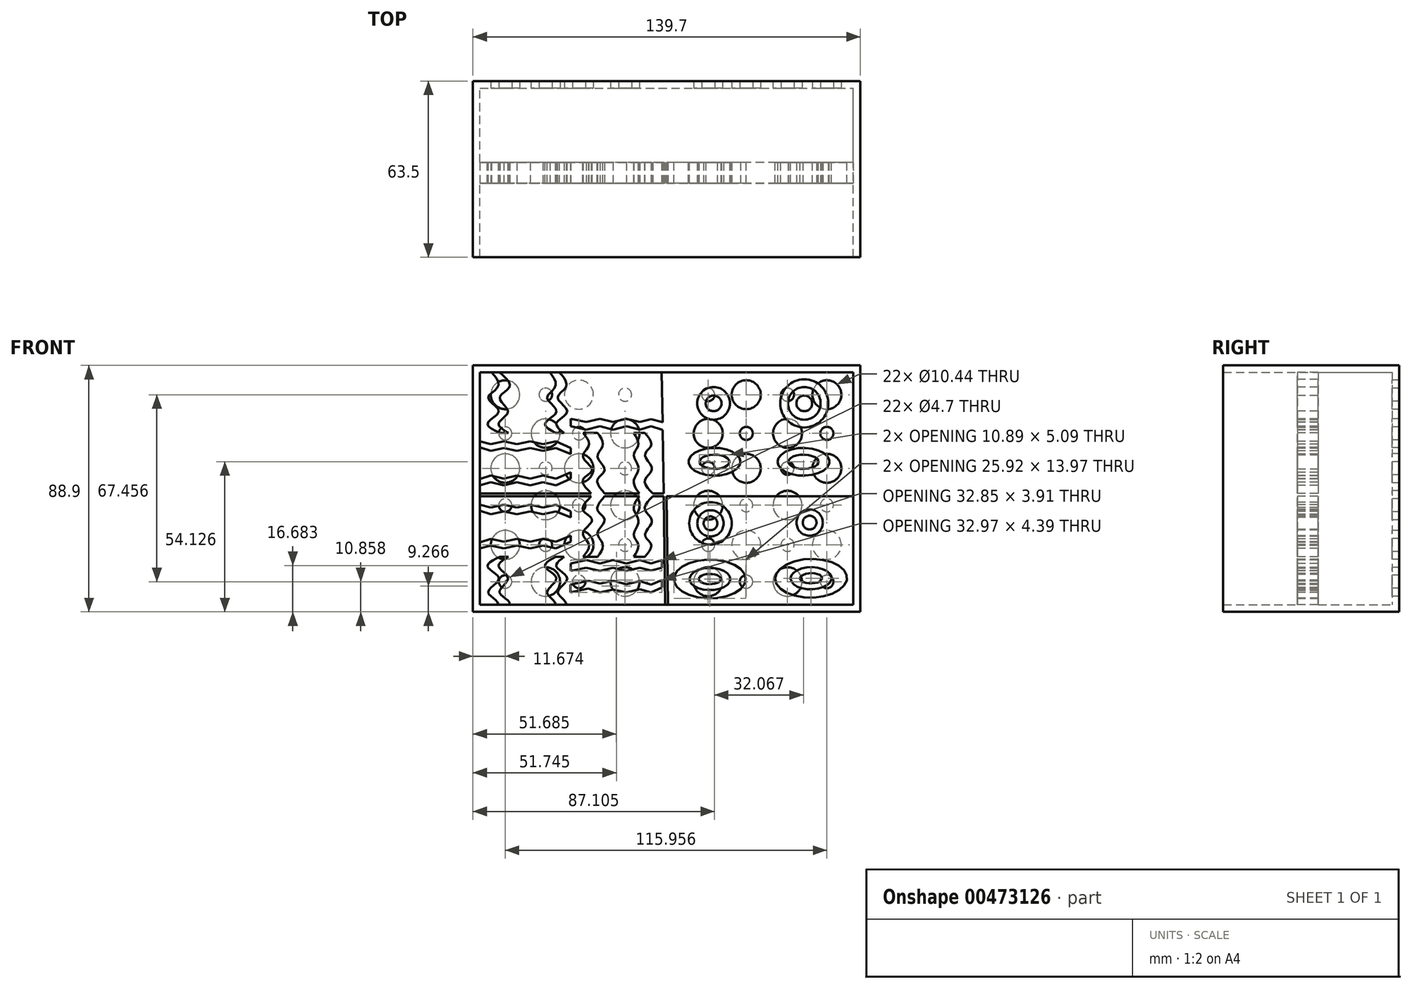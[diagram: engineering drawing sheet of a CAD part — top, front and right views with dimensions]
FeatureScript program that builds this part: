
annotation { "Feature Type Name" : "Feature", "Feature Type Description" : "" }
export const myFeature = defineFeature(function(context is Context, id is Id, definition is map)
    precondition{}
    {
        {
            var Q0;
            Q0=qCreatedBy(makeId("Front.planeOp"),FACE);
            var sketch = newSketch(context, id + "F0", { "sketchPlane" : qUnion([Q0])});
            skLineSegment(sketch, "E0.bottom", {"start": v(-68.61, 46.72) * mm, "end": v(71.09, 46.72) * mm});
            skLineSegment(sketch, "E0.top", {"start": v(-68.61, -42.18) * mm, "end": v(71.09, -42.18) * mm});
            skLineSegment(sketch, "E0.left", {"start": v(-68.61, 46.72) * mm, "end": v(-68.61, -42.18) * mm});
            skLineSegment(sketch, "E0.right", {"start": v(71.09, 46.72) * mm, "end": v(71.09, -42.18) * mm});
            skSolve(sketch);
        }
        {
            var Q0;
            Q0=makeQuery(id+"F0.imprint","IMPRINT",FACE,{"disambiguationData":[TD([[makeQuery(id+"F0.imprint","IMPRINT",EDGE,{"derivedFrom":sQuery(id+"F0.wireOp",EDGE,"E0.bottom")}),-1.0]])]});
            extrude(context, id + "F1", {"entities" : qUnion([Q0]), "depth" : 63.5 * mm});
        }
        {
            var Q0;
            Q0=makeQuery(id+"F1.opExtrude","CAP_FACE",FACE,{"disambiguationData":[OSD([sQuery(id+"F0.wireOp",EDGE,"E0.bottom"),sQuery(id+"F0.wireOp",EDGE,"E0.top"),sQuery(id+"F0.wireOp",EDGE,"E0.left"),sQuery(id+"F0.wireOp",EDGE,"E0.right")])],"isStart":false});
            shell(context, id + "F2", {"entities" : qUnion([Q0]), "thickness" : 2.54 * mm});
        }
        {
            var Q0;
            Q0=makeQuery(id+"F2.opShell","OFFSET_FACE",FACE,{"disambiguationData":[OSD([sQuery(id+"F0.wireOp",EDGE,"E0.bottom"),sQuery(id+"F0.wireOp",EDGE,"E0.top"),sQuery(id+"F0.wireOp",EDGE,"E0.left"),sQuery(id+"F0.wireOp",EDGE,"E0.right")])]});
            var sketch = newSketch(context, id + "F3", { "sketchPlane" : qUnion([Q0])});
            skLineSegment(sketch, "E1", {"start": v(-66.07, 2.27) * mm, "end": v(68.55, 2.27) * mm});
            skLineSegment(sketch, "E2", {"start": v(1.24, 44.18) * mm, "end": v(1.24, -39.64) * mm});
            skCircle(sketch, "E3", {"center": v(-56.94, 36.13) * mm, "radius": 5.21 * mm});
            skCircle(sketch, "E4", {"center": v(-42.4, 36.13) * mm, "radius": 2.36 * mm});
            skCircle(sketch, "E5", {"center": v(-30.37, 36.13) * mm, "radius": 5.22 * mm});
            skCircle(sketch, "E6", {"center": v(-13.75, 36.13) * mm, "radius": 2.36 * mm});
            skCircle(sketch, "E7", {"center": v(-56.94, 22.18) * mm, "radius": 2.35 * mm});
            skCircle(sketch, "E8", {"center": v(-42.4, 22.18) * mm, "radius": 5.22 * mm});
            skCircle(sketch, "E9", {"center": v(-30.37, 22.18) * mm, "radius": 2.35 * mm});
            skCircle(sketch, "E10", {"center": v(-13.75, 22.18) * mm, "radius": 5.22 * mm});
            skCircle(sketch, "E11", {"center": v(-56.94, 9.59) * mm, "radius": 5.22 * mm});
            skCircle(sketch, "E12", {"center": v(-42.4, 9.59) * mm, "radius": 2.35 * mm});
            skCircle(sketch, "E13", {"center": v(-30.37, 9.59) * mm, "radius": 5.22 * mm});
            skCircle(sketch, "E14", {"center": v(-13.75, 9.59) * mm, "radius": 2.35 * mm});
            skCircle(sketch, "E15", {"center": v(-56.94, -3.73) * mm, "radius": 2.35 * mm});
            skCircle(sketch, "E16", {"center": v(-42.4, -3.73) * mm, "radius": 5.22 * mm});
            skCircle(sketch, "E17", {"center": v(-30.37, -3.73) * mm, "radius": 2.35 * mm});
            skCircle(sketch, "E18", {"center": v(-13.75, -3.73) * mm, "radius": 5.22 * mm});
            skCircle(sketch, "E19", {"center": v(-56.94, -18.04) * mm, "radius": 5.22 * mm});
            skCircle(sketch, "E20", {"center": v(-42.4, -18.04) * mm, "radius": 2.35 * mm});
            skCircle(sketch, "E21", {"center": v(-30.37, -18.04) * mm, "radius": 5.22 * mm});
            skCircle(sketch, "E22", {"center": v(-13.75, -18.04) * mm, "radius": 2.35 * mm});
            skCircle(sketch, "E23", {"center": v(-56.94, -31.32) * mm, "radius": 2.35 * mm});
            skCircle(sketch, "E24", {"center": v(-42.4, -31.32) * mm, "radius": 5.22 * mm});
            skCircle(sketch, "E25", {"center": v(-30.37, -31.32) * mm, "radius": 2.35 * mm});
            skCircle(sketch, "E26", {"center": v(-13.75, -31.32) * mm, "radius": 5.22 * mm});
            skCircle(sketch, "E27", {"center": v(16.23, 36.13) * mm, "radius": 2.35 * mm});
            skCircle(sketch, "E28", {"center": v(29.95, 36.13) * mm, "radius": 5.22 * mm});
            skCircle(sketch, "E29", {"center": v(44.83, 36.13) * mm, "radius": 2.35 * mm});
            skCircle(sketch, "E30", {"center": v(59.02, 36.13) * mm, "radius": 5.22 * mm});
            skCircle(sketch, "E31", {"center": v(16.23, 22.18) * mm, "radius": 5.22 * mm});
            skCircle(sketch, "E32", {"center": v(29.95, 22.18) * mm, "radius": 2.35 * mm});
            skCircle(sketch, "E33", {"center": v(44.83, 22.18) * mm, "radius": 5.22 * mm});
            skCircle(sketch, "E34", {"center": v(59.02, 22.18) * mm, "radius": 2.35 * mm});
            skCircle(sketch, "E35", {"center": v(16.23, 9.59) * mm, "radius": 2.35 * mm});
            skCircle(sketch, "E36", {"center": v(29.95, 9.59) * mm, "radius": 5.22 * mm});
            skCircle(sketch, "E37", {"center": v(44.83, 9.59) * mm, "radius": 2.35 * mm});
            skCircle(sketch, "E38", {"center": v(59.02, 9.59) * mm, "radius": 5.22 * mm});
            skCircle(sketch, "E39", {"center": v(16.23, -3.73) * mm, "radius": 5.22 * mm});
            skCircle(sketch, "E40", {"center": v(29.95, -3.73) * mm, "radius": 2.35 * mm});
            skCircle(sketch, "E41", {"center": v(44.83, -3.73) * mm, "radius": 5.22 * mm});
            skCircle(sketch, "E42", {"center": v(59.02, -3.73) * mm, "radius": 2.35 * mm});
            skCircle(sketch, "E43", {"center": v(16.23, -18.04) * mm, "radius": 2.35 * mm});
            skCircle(sketch, "E44", {"center": v(29.95, -18.04) * mm, "radius": 5.22 * mm});
            skCircle(sketch, "E45", {"center": v(44.83, -18.04) * mm, "radius": 2.35 * mm});
            skCircle(sketch, "E46", {"center": v(59.02, -18.04) * mm, "radius": 5.22 * mm});
            skCircle(sketch, "E47", {"center": v(16.23, -31.32) * mm, "radius": 5.22 * mm});
            skCircle(sketch, "E48", {"center": v(29.95, -31.32) * mm, "radius": 2.35 * mm});
            skCircle(sketch, "E49", {"center": v(44.83, -31.32) * mm, "radius": 5.22 * mm});
            skCircle(sketch, "E50", {"center": v(59.02, -31.32) * mm, "radius": 2.35 * mm});
            skSolve(sketch);
        }
        {
            var Q0;
            Q0=makeQuery(id+"F3.imprint","IMPRINT",FACE,{"disambiguationData":[TD([[makeQuery(id+"F3.imprint","IMPRINT",EDGE,{"derivedFrom":sQuery(id+"F3.wireOp",EDGE,"E3")}),1.0]])]});
            var Q1;
            Q1=makeQuery(id+"F3.imprint","IMPRINT",FACE,{"disambiguationData":[TD([[makeQuery(id+"F3.imprint","IMPRINT",EDGE,{"derivedFrom":sQuery(id+"F3.wireOp",EDGE,"E4")}),1.0]])]});
            var Q2;
            Q2=makeQuery(id+"F3.imprint","IMPRINT",FACE,{"disambiguationData":[TD([[makeQuery(id+"F3.imprint","IMPRINT",EDGE,{"derivedFrom":sQuery(id+"F3.wireOp",EDGE,"E5")}),1.0]])]});
            var Q3;
            Q3=makeQuery(id+"F3.imprint","IMPRINT",FACE,{"disambiguationData":[TD([[makeQuery(id+"F3.imprint","IMPRINT",EDGE,{"derivedFrom":sQuery(id+"F3.wireOp",EDGE,"E6")}),1.0]])]});
            var Q4;
            Q4=makeQuery(id+"F3.imprint","IMPRINT",FACE,{"disambiguationData":[TD([[makeQuery(id+"F3.imprint","IMPRINT",EDGE,{"derivedFrom":sQuery(id+"F3.wireOp",EDGE,"E10")}),1.0]])]});
            var Q5;
            Q5=makeQuery(id+"F3.imprint","IMPRINT",FACE,{"disambiguationData":[TD([[makeQuery(id+"F3.imprint","IMPRINT",EDGE,{"derivedFrom":sQuery(id+"F3.wireOp",EDGE,"E9")}),1.0]])]});
            var Q6;
            Q6=makeQuery(id+"F3.imprint","IMPRINT",FACE,{"disambiguationData":[TD([[makeQuery(id+"F3.imprint","IMPRINT",EDGE,{"derivedFrom":sQuery(id+"F3.wireOp",EDGE,"E8")}),1.0]])]});
            var Q7;
            Q7=makeQuery(id+"F3.imprint","IMPRINT",FACE,{"disambiguationData":[TD([[makeQuery(id+"F3.imprint","IMPRINT",EDGE,{"derivedFrom":sQuery(id+"F3.wireOp",EDGE,"E7")}),1.0]])]});
            var Q8;
            Q8=makeQuery(id+"F3.imprint","IMPRINT",FACE,{"disambiguationData":[TD([[makeQuery(id+"F3.imprint","IMPRINT",EDGE,{"derivedFrom":sQuery(id+"F3.wireOp",EDGE,"E11")}),1.0]])]});
            var Q9;
            Q9=makeQuery(id+"F3.imprint","IMPRINT",FACE,{"disambiguationData":[TD([[makeQuery(id+"F3.imprint","IMPRINT",EDGE,{"derivedFrom":sQuery(id+"F3.wireOp",EDGE,"E12")}),1.0]])]});
            var Q10;
            Q10=makeQuery(id+"F3.imprint","IMPRINT",FACE,{"disambiguationData":[TD([[makeQuery(id+"F3.imprint","IMPRINT",EDGE,{"derivedFrom":sQuery(id+"F3.wireOp",EDGE,"E13")}),1.0]])]});
            var Q11;
            Q11=makeQuery(id+"F3.imprint","IMPRINT",FACE,{"disambiguationData":[TD([[makeQuery(id+"F3.imprint","IMPRINT",EDGE,{"derivedFrom":sQuery(id+"F3.wireOp",EDGE,"E14")}),1.0]])]});
            var Q12;
            Q12=makeQuery(id+"F3.imprint","IMPRINT",FACE,{"disambiguationData":[TD([[makeQuery(id+"F3.imprint","IMPRINT",EDGE,{"derivedFrom":sQuery(id+"F3.wireOp",EDGE,"E15")}),1.0]])]});
            var Q13;
            Q13=makeQuery(id+"F3.imprint","IMPRINT",FACE,{"disambiguationData":[TD([[makeQuery(id+"F3.imprint","IMPRINT",EDGE,{"derivedFrom":sQuery(id+"F3.wireOp",EDGE,"E16")}),1.0]])]});
            var Q14;
            Q14=makeQuery(id+"F3.imprint","IMPRINT",FACE,{"disambiguationData":[TD([[makeQuery(id+"F3.imprint","IMPRINT",EDGE,{"derivedFrom":sQuery(id+"F3.wireOp",EDGE,"E17")}),1.0]])]});
            var Q15;
            Q15=makeQuery(id+"F3.imprint","IMPRINT",FACE,{"disambiguationData":[TD([[makeQuery(id+"F3.imprint","IMPRINT",EDGE,{"derivedFrom":sQuery(id+"F3.wireOp",EDGE,"E18")}),1.0]])]});
            var Q16;
            Q16=makeQuery(id+"F3.imprint","IMPRINT",FACE,{"disambiguationData":[TD([[makeQuery(id+"F3.imprint","IMPRINT",EDGE,{"derivedFrom":sQuery(id+"F3.wireOp",EDGE,"E19")}),1.0]])]});
            var Q17;
            Q17=makeQuery(id+"F3.imprint","IMPRINT",FACE,{"disambiguationData":[TD([[makeQuery(id+"F3.imprint","IMPRINT",EDGE,{"derivedFrom":sQuery(id+"F3.wireOp",EDGE,"E20")}),1.0]])]});
            var Q18;
            Q18=makeQuery(id+"F3.imprint","IMPRINT",FACE,{"disambiguationData":[TD([[makeQuery(id+"F3.imprint","IMPRINT",EDGE,{"derivedFrom":sQuery(id+"F3.wireOp",EDGE,"E21")}),1.0]])]});
            var Q19;
            Q19=makeQuery(id+"F3.imprint","IMPRINT",FACE,{"disambiguationData":[TD([[makeQuery(id+"F3.imprint","IMPRINT",EDGE,{"derivedFrom":sQuery(id+"F3.wireOp",EDGE,"E22")}),1.0]])]});
            var Q20;
            Q20=makeQuery(id+"F3.imprint","IMPRINT",FACE,{"disambiguationData":[TD([[makeQuery(id+"F3.imprint","IMPRINT",EDGE,{"derivedFrom":sQuery(id+"F3.wireOp",EDGE,"E23")}),1.0]])]});
            var Q21;
            Q21=makeQuery(id+"F3.imprint","IMPRINT",FACE,{"disambiguationData":[TD([[makeQuery(id+"F3.imprint","IMPRINT",EDGE,{"derivedFrom":sQuery(id+"F3.wireOp",EDGE,"E24")}),1.0]])]});
            var Q22;
            Q22=makeQuery(id+"F3.imprint","IMPRINT",FACE,{"disambiguationData":[TD([[makeQuery(id+"F3.imprint","IMPRINT",EDGE,{"derivedFrom":sQuery(id+"F3.wireOp",EDGE,"E25")}),1.0]])]});
            var Q23;
            Q23=makeQuery(id+"F3.imprint","IMPRINT",FACE,{"disambiguationData":[TD([[makeQuery(id+"F3.imprint","IMPRINT",EDGE,{"derivedFrom":sQuery(id+"F3.wireOp",EDGE,"E26")}),1.0]])]});
            var Q24;
            Q24=makeQuery(id+"F3.imprint","IMPRINT",FACE,{"disambiguationData":[TD([[makeQuery(id+"F3.imprint","IMPRINT",EDGE,{"derivedFrom":sQuery(id+"F3.wireOp",EDGE,"E27")}),1.0]])]});
            var Q25;
            Q25=makeQuery(id+"F3.imprint","IMPRINT",FACE,{"disambiguationData":[TD([[makeQuery(id+"F3.imprint","IMPRINT",EDGE,{"derivedFrom":sQuery(id+"F3.wireOp",EDGE,"E31")}),1.0]])]});
            var Q26;
            Q26=makeQuery(id+"F3.imprint","IMPRINT",FACE,{"disambiguationData":[TD([[makeQuery(id+"F3.imprint","IMPRINT",EDGE,{"derivedFrom":sQuery(id+"F3.wireOp",EDGE,"E35")}),1.0]])]});
            var Q27;
            Q27=makeQuery(id+"F3.imprint","IMPRINT",FACE,{"disambiguationData":[TD([[makeQuery(id+"F3.imprint","IMPRINT",EDGE,{"derivedFrom":sQuery(id+"F3.wireOp",EDGE,"E36")}),1.0]])]});
            var Q28;
            Q28=makeQuery(id+"F3.imprint","IMPRINT",FACE,{"disambiguationData":[TD([[makeQuery(id+"F3.imprint","IMPRINT",EDGE,{"derivedFrom":sQuery(id+"F3.wireOp",EDGE,"E32")}),1.0]])]});
            var Q29;
            Q29=makeQuery(id+"F3.imprint","IMPRINT",FACE,{"disambiguationData":[TD([[makeQuery(id+"F3.imprint","IMPRINT",EDGE,{"derivedFrom":sQuery(id+"F3.wireOp",EDGE,"E28")}),1.0]])]});
            var Q30;
            Q30=makeQuery(id+"F3.imprint","IMPRINT",FACE,{"disambiguationData":[TD([[makeQuery(id+"F3.imprint","IMPRINT",EDGE,{"derivedFrom":sQuery(id+"F3.wireOp",EDGE,"E29")}),1.0]])]});
            var Q31;
            Q31=makeQuery(id+"F3.imprint","IMPRINT",FACE,{"disambiguationData":[TD([[makeQuery(id+"F3.imprint","IMPRINT",EDGE,{"derivedFrom":sQuery(id+"F3.wireOp",EDGE,"E33")}),1.0]])]});
            var Q32;
            Q32=makeQuery(id+"F3.imprint","IMPRINT",FACE,{"disambiguationData":[TD([[makeQuery(id+"F3.imprint","IMPRINT",EDGE,{"derivedFrom":sQuery(id+"F3.wireOp",EDGE,"E37")}),1.0]])]});
            var Q33;
            Q33=makeQuery(id+"F3.imprint","IMPRINT",FACE,{"disambiguationData":[TD([[makeQuery(id+"F3.imprint","IMPRINT",EDGE,{"derivedFrom":sQuery(id+"F3.wireOp",EDGE,"E38")}),1.0]])]});
            var Q34;
            Q34=makeQuery(id+"F3.imprint","IMPRINT",FACE,{"disambiguationData":[TD([[makeQuery(id+"F3.imprint","IMPRINT",EDGE,{"derivedFrom":sQuery(id+"F3.wireOp",EDGE,"E34")}),1.0]])]});
            var Q35;
            Q35=makeQuery(id+"F3.imprint","IMPRINT",FACE,{"disambiguationData":[TD([[makeQuery(id+"F3.imprint","IMPRINT",EDGE,{"derivedFrom":sQuery(id+"F3.wireOp",EDGE,"E30")}),1.0]])]});
            var Q36;
            Q36=makeQuery(id+"F3.imprint","IMPRINT",FACE,{"disambiguationData":[TD([[makeQuery(id+"F3.imprint","IMPRINT",EDGE,{"derivedFrom":sQuery(id+"F3.wireOp",EDGE,"E39")}),1.0]])]});
            var Q37;
            Q37=makeQuery(id+"F3.imprint","IMPRINT",FACE,{"disambiguationData":[TD([[makeQuery(id+"F3.imprint","IMPRINT",EDGE,{"derivedFrom":sQuery(id+"F3.wireOp",EDGE,"E47")}),1.0]])]});
            var Q38;
            Q38=makeQuery(id+"F3.imprint","IMPRINT",FACE,{"disambiguationData":[TD([[makeQuery(id+"F3.imprint","IMPRINT",EDGE,{"derivedFrom":sQuery(id+"F3.wireOp",EDGE,"E43")}),1.0]])]});
            var Q39;
            Q39=makeQuery(id+"F3.imprint","IMPRINT",FACE,{"disambiguationData":[TD([[makeQuery(id+"F3.imprint","IMPRINT",EDGE,{"derivedFrom":sQuery(id+"F3.wireOp",EDGE,"E40")}),1.0]])]});
            var Q40;
            Q40=makeQuery(id+"F3.imprint","IMPRINT",FACE,{"disambiguationData":[TD([[makeQuery(id+"F3.imprint","IMPRINT",EDGE,{"derivedFrom":sQuery(id+"F3.wireOp",EDGE,"E44")}),1.0]])]});
            var Q41;
            Q41=makeQuery(id+"F3.imprint","IMPRINT",FACE,{"disambiguationData":[TD([[makeQuery(id+"F3.imprint","IMPRINT",EDGE,{"derivedFrom":sQuery(id+"F3.wireOp",EDGE,"E48")}),1.0]])]});
            var Q42;
            Q42=makeQuery(id+"F3.imprint","IMPRINT",FACE,{"disambiguationData":[TD([[makeQuery(id+"F3.imprint","IMPRINT",EDGE,{"derivedFrom":sQuery(id+"F3.wireOp",EDGE,"E49")}),1.0]])]});
            var Q43;
            Q43=makeQuery(id+"F3.imprint","IMPRINT",FACE,{"disambiguationData":[TD([[makeQuery(id+"F3.imprint","IMPRINT",EDGE,{"derivedFrom":sQuery(id+"F3.wireOp",EDGE,"E45")}),1.0]])]});
            var Q44;
            Q44=makeQuery(id+"F3.imprint","IMPRINT",FACE,{"disambiguationData":[TD([[makeQuery(id+"F3.imprint","IMPRINT",EDGE,{"derivedFrom":sQuery(id+"F3.wireOp",EDGE,"E41")}),1.0]])]});
            var Q45;
            Q45=makeQuery(id+"F3.imprint","IMPRINT",FACE,{"disambiguationData":[TD([[makeQuery(id+"F3.imprint","IMPRINT",EDGE,{"derivedFrom":sQuery(id+"F3.wireOp",EDGE,"E42")}),1.0]])]});
            var Q46;
            Q46=makeQuery(id+"F3.imprint","IMPRINT",FACE,{"disambiguationData":[TD([[makeQuery(id+"F3.imprint","IMPRINT",EDGE,{"derivedFrom":sQuery(id+"F3.wireOp",EDGE,"E46")}),1.0]])]});
            var Q47;
            Q47=makeQuery(id+"F3.imprint","IMPRINT",FACE,{"disambiguationData":[TD([[makeQuery(id+"F3.imprint","IMPRINT",EDGE,{"derivedFrom":sQuery(id+"F3.wireOp",EDGE,"E50")}),1.0]])]});
            extrude(context, id + "F4", {"entities" : qUnion([Q0, Q1, Q2, Q3, Q4, Q5, Q6, Q7, Q8, Q9, Q10, Q11, Q12, Q13, Q14, Q15, Q16, Q17, Q18, Q19, Q20, Q21, Q22, Q23, Q24, Q25, Q26, Q27, Q28, Q29, Q30, Q31, Q32, Q33, Q34, Q35, Q36, Q37, Q38, Q39, Q40, Q41, Q42, Q43, Q44, Q45, Q46, Q47]), "operationType" : NewBodyOperationType.REMOVE, "oppositeDirection" : true, "depth" : 25.4 * mm});
        }
        {
            var Q0;
            Q0=makeQuery(id+"F2.opShell","OFFSET_FACE",FACE,{"disambiguationData":[OSD([sQuery(id+"F0.wireOp",EDGE,"E0.top")])]});
            var sketch = newSketch(context, id + "F5", { "sketchPlane" : qUnion([Q0])});
            skLineSegment(sketch, "E51", {"start": v(68.55, -36.8) * mm, "end": v(-66.07, -36.8) * mm});
            skLineSegment(sketch, "E52", {"start": v(68.55, -29.26) * mm, "end": v(-66.07, -29.26) * mm});
            skSolve(sketch);
        }
        {
            var Q0;
            {var subQ0=sQuery(id+"F5.wireOp",EDGE,"E51");Q0=makeQuery(id+"F5.imprint","IMPRINT",FACE,{"disambiguationData":[TD([[makeQuery(id+"F5.imprint","IMPRINT",EDGE,{"derivedFrom":subQ0}),-1.0]])]});}
            extrude(context, id + "F6", {"entities" : qUnion([Q0]), "operationType" : NewBodyOperationType.ADD, "endBound" : BoundingType.UP_TO_NEXT, "depth" : 25.4 * mm});
        }
        {
            var Q0;
            Q0=makeQuery(id+"F6.opExtrude","SWEPT_FACE",FACE,{"disambiguationData":[OSD([sQuery(id+"F5.wireOp",EDGE,"E51")])]});
            var sketch = newSketch(context, id + "F7", { "sketchPlane" : qUnion([Q0])});
            skLineSegment(sketch, "E53", {"start": v(-66.07, 0.5) * mm, "end": v(0.14, 0.5) * mm});
            skLineSegment(sketch, "E54", {"start": v(-66.07, -0.5) * mm, "end": v(0.15, -0.5) * mm});
            skLineSegment(sketch, "E55", {"start": v(0.5, 44.18) * mm, "end": v(1.15, 0.5) * mm});
            skLineSegment(sketch, "E56", {"start": v(0.73, -39.64) * mm, "end": v(0.15, -0.5) * mm});
            skLineSegment(sketch, "E57.trimOffspring", {"start": v(0.14, 0.5) * mm, "end": v(-0.5, 44.18) * mm});
            skLineSegment(sketch, "E58.trimOffspring", {"start": v(1.17, -0.5) * mm, "end": v(1.75, -39.64) * mm});
            skLineSegment(sketch, "E59.trimOffspring", {"start": v(1.15, 0.5) * mm, "end": v(68.55, 0.5) * mm});
            skLineSegment(sketch, "E60.trimOffspring", {"start": v(1.17, -0.5) * mm, "end": v(68.55, -0.5) * mm});
            skLineSegment(sketch, "E61", {"start": v(-0.5, 44.18) * mm, "end": v(0.5, 44.18) * mm});
            skLineSegment(sketch, "E62", {"start": v(-66.07, 0.5) * mm, "end": v(-66.07, -0.5) * mm});
            skLineSegment(sketch, "E63", {"start": v(0.73, -39.64) * mm, "end": v(1.75, -39.64) * mm});
            skLineSegment(sketch, "E64", {"start": v(68.55, 0.5) * mm, "end": v(68.55, -0.5) * mm});
            skSolve(sketch);
        }
        {
            var Q0;
            Q0=makeQuery(id+"F7.imprint","IMPRINT",FACE,{"disambiguationData":[TD([[makeQuery(id+"F7.imprint","IMPRINT",EDGE,{"derivedFrom":sQuery(id+"F7.wireOp",EDGE,"E53")}),-1.0]])]});
            extrude(context, id + "F8", {"entities" : qUnion([Q0]), "operationType" : NewBodyOperationType.REMOVE, "endBound" : BoundingType.UP_TO_NEXT, "oppositeDirection" : true, "depth" : 25.4 * mm});
        }
        {
            var Q0;
            Q0=makeQuery(id+"F8.boolean.opBoolean","SPLIT",FACE,{"disambiguationData":[TD([makeQuery(id+"F8.opExtrude","SWEPT_FACE",FACE,{"disambiguationData":[OSD([sQuery(id+"F7.wireOp",EDGE,"E53")])]})])],"derivedFrom":makeQuery(id+"F6.opExtrude","SWEPT_FACE",FACE,{"disambiguationData":[OSD([sQuery(id+"F5.wireOp",EDGE,"E51")])]})});
            var sketch = newSketch(context, id + "F9", { "sketchPlane" : qUnion([Q0])});
            skLineSegment(sketch, "E65", {"start": v(-33.29, 44.18) * mm, "end": v(-33.29, 0.5) * mm});
            skLineSegment(sketch, "E66", {"start": v(-66.07, 22.34) * mm, "end": v(-0.19, 22.34) * mm});
            skFitSpline(sketch, "E67", {"points": [v(-61.87, 44.18) * mm, v(-59.58, 39) * mm, v(-63.11, 35) * mm, v(-59.3, 30.13) * mm, v(-63.3, 25.92) * mm, v(-58.9, 22.34) * mm], "startDerivative": vector(23.2, -23.73) * mm, "endDerivative": vector(36.7, -17.38) * mm});
            skLineSegment(sketch, "E68", {"start": v(-61.87, 44.18) * mm, "end": v(-59, 44.18) * mm});
            skFitSpline(sketch, "E69", {"points": [v(-59, 44.18) * mm, v(-55.38, 38.9) * mm, v(-59, 35) * mm, v(-55.95, 30.13) * mm, v(-59.3, 25.92) * mm, v(-55.85, 22.34) * mm], "startDerivative": vector(30.05, -26.16) * mm, "endDerivative": vector(30.43, -18.57) * mm});
            skLineSegment(sketch, "E70", {"start": v(-58.9, 22.34) * mm, "end": v(-55.85, 22.34) * mm});
            skLineSegment(sketch, "E71", {"start": v(-37.48, 44.18) * mm, "end": v(-40.86, 44.18) * mm});
            skFitSpline(sketch, "E72", {"points": [v(-40.86, 44.18) * mm, v(-38.93, 39) * mm, v(-41.88, 35) * mm, v(-38.47, 30.13) * mm, v(-42.56, 25.92) * mm, v(-38.8, 22.34) * mm], "startDerivative": vector(19.63, -23.54) * mm, "endDerivative": vector(32.62, -18.1) * mm});
            skFitSpline(sketch, "E73", {"points": [v(-37.48, 44.18) * mm, v(-35.02, 39) * mm, v(-38.03, 35) * mm, v(-34.59, 30.13) * mm, v(-38.47, 25.92) * mm, v(-35.78, 22.34) * mm], "startDerivative": vector(22.76, -22.6) * mm, "endDerivative": vector(26.2, -19.57) * mm});
            skLineSegment(sketch, "E74", {"start": v(-38.8, 22.34) * mm, "end": v(-35.78, 22.34) * mm});
            skLineSegment(sketch, "E75", {"start": v(-66.07, 3.5) * mm, "end": v(-66.07, 5.7) * mm});
            skLineSegment(sketch, "E76", {"start": v(-66.07, 3.5) * mm, "end": v(-62.16, 4.6) * mm});
            skPoint(sketch, "E76.endSnap0", {"position": v(-66.07, 4.6) * mm});
            skLineSegment(sketch, "E77", {"start": v(-62.16, 4.6) * mm, "end": v(-57.43, 3.5) * mm});
            skLineSegment(sketch, "E78", {"start": v(-57.43, 3.5) * mm, "end": v(-52.7, 4.6) * mm});
            skLineSegment(sketch, "E79", {"start": v(-52.7, 4.6) * mm, "end": v(-47.98, 3.5) * mm});
            skLineSegment(sketch, "E80", {"start": v(-47.98, 3.5) * mm, "end": v(-43.39, 4.6) * mm});
            skLineSegment(sketch, "E81", {"start": v(-43.39, 4.6) * mm, "end": v(-38.66, 3.5) * mm});
            skLineSegment(sketch, "E82", {"start": v(-38.66, 3.5) * mm, "end": v(-33.29, 5.9) * mm});
            skLineSegment(sketch, "E83", {"start": v(-33.29, 5.9) * mm, "end": v(-33.29, 8.14) * mm});
            skLineSegment(sketch, "E84", {"start": v(-33.29, 8.14) * mm, "end": v(-38.66, 5.9) * mm});
            skLineSegment(sketch, "E85", {"start": v(-38.66, 5.9) * mm, "end": v(-43.39, 7.01) * mm});
            skLineSegment(sketch, "E86", {"start": v(-43.39, 7.01) * mm, "end": v(-47.98, 5.9) * mm});
            skLineSegment(sketch, "E87", {"start": v(-47.98, 5.9) * mm, "end": v(-52.7, 7.01) * mm});
            skLineSegment(sketch, "E88", {"start": v(-52.7, 7.01) * mm, "end": v(-57.43, 5.9) * mm});
            skLineSegment(sketch, "E89", {"start": v(-57.43, 5.9) * mm, "end": v(-62.16, 7.01) * mm});
            skLineSegment(sketch, "E90", {"start": v(-62.16, 7.01) * mm, "end": v(-66.07, 5.7) * mm});
            skLineSegment(sketch, "E91.MirrorCS", {"start": v(-33.29, 14.7) * mm, "end": v(-38.66, 16.94) * mm});
            skLineSegment(sketch, "E92.MirrorCS", {"start": v(-38.66, 19.35) * mm, "end": v(-33.29, 16.94) * mm});
            skLineSegment(sketch, "E93.MirrorCS", {"start": v(-43.39, 18.24) * mm, "end": v(-38.66, 19.35) * mm});
            skLineSegment(sketch, "E94.MirrorCS", {"start": v(-38.66, 16.94) * mm, "end": v(-43.39, 15.83) * mm});
            skLineSegment(sketch, "E95.MirrorCS", {"start": v(-43.39, 15.83) * mm, "end": v(-47.98, 16.94) * mm});
            skLineSegment(sketch, "E96.MirrorCS", {"start": v(-47.98, 19.35) * mm, "end": v(-43.39, 18.24) * mm});
            skLineSegment(sketch, "E97.MirrorCS", {"start": v(-52.7, 18.24) * mm, "end": v(-47.98, 19.35) * mm});
            skLineSegment(sketch, "E98.MirrorCS", {"start": v(-47.98, 16.94) * mm, "end": v(-52.7, 15.83) * mm});
            skLineSegment(sketch, "E99.MirrorCS", {"start": v(-52.7, 15.83) * mm, "end": v(-57.43, 16.94) * mm});
            skLineSegment(sketch, "E100.MirrorCS", {"start": v(-57.43, 19.35) * mm, "end": v(-52.7, 18.24) * mm});
            skLineSegment(sketch, "E101.MirrorCS", {"start": v(-57.43, 16.94) * mm, "end": v(-62.16, 15.83) * mm});
            skLineSegment(sketch, "E102.MirrorCS", {"start": v(-62.16, 18.24) * mm, "end": v(-57.43, 19.35) * mm});
            skLineSegment(sketch, "E103.MirrorCS", {"start": v(-66.07, 19.35) * mm, "end": v(-62.16, 18.24) * mm});
            skLineSegment(sketch, "E104.MirrorCS", {"start": v(-62.16, 15.83) * mm, "end": v(-66.07, 17.14) * mm});
            skLineSegment(sketch, "E105.MirrorCS", {"start": v(-66.07, 19.35) * mm, "end": v(-66.07, 17.14) * mm});
            skLineSegment(sketch, "E106.MirrorCS", {"start": v(-33.29, 16.94) * mm, "end": v(-33.29, 14.7) * mm});
            skLineSegment(sketch, "E107", {"start": v(-33.29, 41.18) * mm, "end": v(-33.29, 38.48) * mm});
            skLineSegment(sketch, "E108", {"start": v(-33.29, 38.48) * mm, "end": v(-27.72, 39.68) * mm});
            skLineSegment(sketch, "E109", {"start": v(-33.29, 41.18) * mm, "end": v(-27.72, 42.38) * mm});
            skLineSegment(sketch, "E110", {"start": v(-27.72, 39.68) * mm, "end": v(-22.84, 38.48) * mm});
            skLineSegment(sketch, "E111", {"start": v(-27.72, 42.38) * mm, "end": v(-22.84, 41.18) * mm});
            skLineSegment(sketch, "E112", {"start": v(-22.84, 38.48) * mm, "end": v(-18.15, 39.68) * mm});
            skLineSegment(sketch, "E113", {"start": v(-22.84, 41.18) * mm, "end": v(-18.15, 42.38) * mm});
            skLineSegment(sketch, "E114", {"start": v(-18.15, 39.68) * mm, "end": v(-13.33, 38.48) * mm});
            skLineSegment(sketch, "E115", {"start": v(-18.15, 42.38) * mm, "end": v(-13.33, 41.18) * mm});
            skPoint(sketch, "E116.endSnap0", {"position": v(-15.74, 39.08) * mm});
            skLineSegment(sketch, "E117", {"start": v(-13.33, 41.18) * mm, "end": v(-8.43, 42.38) * mm});
            skLineSegment(sketch, "E118", {"start": v(-13.33, 38.48) * mm, "end": v(-8.43, 39.68) * mm});
            skLineSegment(sketch, "E119", {"start": v(-8.43, 39.68) * mm, "end": v(-4.35, 38.66) * mm});
            skLineSegment(sketch, "E120", {"start": v(-8.43, 42.38) * mm, "end": v(-4.35, 41.18) * mm});
            skLineSegment(sketch, "E121", {"start": v(-4.35, 38.66) * mm, "end": v(-0.44, 39.68) * mm});
            skLineSegment(sketch, "E122", {"start": v(-4.35, 41.18) * mm, "end": v(-0.48, 42.38) * mm});
            skLineSegment(sketch, "E123.MirrorCS", {"start": v(-33.29, 27.45) * mm, "end": v(-27.72, 26.25) * mm});
            skLineSegment(sketch, "E124.MirrorCS", {"start": v(-33.29, 24.74) * mm, "end": v(-27.72, 23.54) * mm});
            skLineSegment(sketch, "E125.MirrorCS", {"start": v(-27.72, 26.25) * mm, "end": v(-22.84, 27.45) * mm});
            skLineSegment(sketch, "E126.MirrorCS", {"start": v(-27.72, 23.54) * mm, "end": v(-22.84, 24.74) * mm});
            skLineSegment(sketch, "E127.MirrorCS", {"start": v(-22.84, 24.74) * mm, "end": v(-18.15, 23.54) * mm});
            skLineSegment(sketch, "E128.MirrorCS", {"start": v(-22.84, 27.45) * mm, "end": v(-18.15, 26.25) * mm});
            skLineSegment(sketch, "E129.MirrorCS", {"start": v(-18.15, 23.54) * mm, "end": v(-13.33, 24.74) * mm});
            skLineSegment(sketch, "E130.MirrorCS", {"start": v(-18.15, 26.25) * mm, "end": v(-13.33, 27.45) * mm});
            skLineSegment(sketch, "E131.MirrorCS", {"start": v(-13.33, 27.45) * mm, "end": v(-8.43, 26.25) * mm});
            skLineSegment(sketch, "E132.MirrorCS", {"start": v(-8.43, 23.54) * mm, "end": v(-4.35, 24.74) * mm});
            skLineSegment(sketch, "E133.MirrorCS", {"start": v(-8.43, 26.25) * mm, "end": v(-4.35, 27.27) * mm});
            skLineSegment(sketch, "E134.MirrorCS", {"start": v(-4.35, 27.27) * mm, "end": v(-0.44, 26.25) * mm});
            skLineSegment(sketch, "E135.MirrorCS", {"start": v(-4.35, 24.74) * mm, "end": v(-0.48, 23.54) * mm});
            skLineSegment(sketch, "E136", {"start": v(-0.48, 23.54) * mm, "end": v(-0.2, 23.44) * mm});
            skLineSegment(sketch, "E137", {"start": v(-0.44, 26.25) * mm, "end": v(-0.24, 26.16) * mm});
            skLineSegment(sketch, "E138", {"start": v(-28.93, 22.34) * mm, "end": v(-23.65, 22.34) * mm});
            skLineSegment(sketch, "E139", {"start": v(-6.6, 22.34) * mm, "end": v(-7.32, 22.34) * mm});
            skFitSpline(sketch, "E140", {"points": [v(-28.93, 22.34) * mm, v(-26.8, 17.84) * mm, v(-28.93, 13.7) * mm, v(-25.63, 9.06) * mm, v(-28.93, 5.57) * mm, v(-25.94, 0.5) * mm], "startDerivative": vector(19.58, -23.39) * mm, "endDerivative": vector(25.84, -25.67) * mm});
            skPoint(sketch, "E141.2.internal.snap0", {"position": v(-25.28, 26.85) * mm});
            skFitSpline(sketch, "E142", {"points": [v(-23.65, 22.34) * mm, v(-21.8, 17.84) * mm, v(-23.65, 13.7) * mm, v(-21.07, 9.06) * mm, v(-23.65, 5.57) * mm, v(-21.14, 0.5) * mm], "startDerivative": vector(16.61, -23.07) * mm, "endDerivative": vector(21.34, -25.36) * mm});
            skLineSegment(sketch, "E143", {"start": v(-25.94, 0.5) * mm, "end": v(-21.14, 0.5) * mm});
            skFitSpline(sketch, "E144", {"points": [v(-6.6, 22.34) * mm, v(-4.37, 17.77) * mm, v(-6.6, 14.36) * mm, v(-4.07, 9.5) * mm, v(-6.6, 5.34) * mm, v(-3.75, 0.5) * mm], "startDerivative": vector(20.02, -24.11) * mm, "endDerivative": vector(23.18, -23.59) * mm});
            skLineSegment(sketch, "E145", {"start": v(-6.6, 22.34) * mm, "end": v(-10.63, 22.34) * mm});
            skFitSpline(sketch, "E146", {"points": [v(-10.63, 22.34) * mm, v(-9.04, 17.77) * mm, v(-10.63, 14.36) * mm, v(-8.91, 9.5) * mm, v(-10.63, 5.12) * mm, v(-8.57, 0.5) * mm], "startDerivative": vector(14.15, -23.8) * mm, "endDerivative": vector(16.57, -22.5) * mm});
            skLineSegment(sketch, "E147", {"start": v(-8.57, 0.5) * mm, "end": v(-3.75, 0.5) * mm});
            skLineSegment(sketch, "E148", {"start": v(-13.33, 24.74) * mm, "end": v(-8.43, 23.54) * mm});
            skLineSegment(sketch, "E149", {"start": v(0, 44.18) * mm, "end": v(1.24, -39.82) * mm});
            skLineSegment(sketch, "E150", {"start": v(-66.07, 0) * mm, "end": v(68.78, 0) * mm});
            skFitSpline(sketch, "E151.MirrorCS", {"points": [v(-61.87, -44.18) * mm, v(-59.58, -39) * mm, v(-63.11, -35) * mm, v(-59.3, -30.13) * mm, v(-63.3, -25.92) * mm, v(-58.9, -22.34) * mm], "startDerivative": vector(23.2, 23.73) * mm, "endDerivative": vector(36.7, 17.38) * mm});
            skFitSpline(sketch, "E152.MirrorCS", {"points": [v(-40.86, -44.18) * mm, v(-38.93, -39) * mm, v(-41.88, -35) * mm, v(-38.47, -30.13) * mm, v(-42.56, -25.92) * mm, v(-38.8, -22.34) * mm], "startDerivative": vector(19.63, 23.54) * mm, "endDerivative": vector(32.62, 18.1) * mm});
            skFitSpline(sketch, "E153.MirrorCS", {"points": [v(-59, -44.18) * mm, v(-55.38, -38.9) * mm, v(-59, -35) * mm, v(-55.95, -30.13) * mm, v(-59.3, -25.92) * mm, v(-55.85, -22.34) * mm], "startDerivative": vector(30.05, 26.16) * mm, "endDerivative": vector(30.43, 18.57) * mm});
            skFitSpline(sketch, "E154.MirrorCS", {"points": [v(-37.48, -44.18) * mm, v(-35.02, -39) * mm, v(-38.03, -35) * mm, v(-34.59, -30.13) * mm, v(-38.47, -25.92) * mm, v(-35.78, -22.34) * mm], "startDerivative": vector(22.76, 22.6) * mm, "endDerivative": vector(26.2, 19.57) * mm});
            skLineSegment(sketch, "E155.MirrorCS", {"start": v(-62.16, -15.83) * mm, "end": v(-66.07, -17.14) * mm});
            skLineSegment(sketch, "E156.MirrorCS", {"start": v(-66.07, -19.35) * mm, "end": v(-62.16, -18.24) * mm});
            skLineSegment(sketch, "E157.MirrorCS", {"start": v(-62.16, -18.24) * mm, "end": v(-57.43, -19.35) * mm});
            skLineSegment(sketch, "E158.MirrorCS", {"start": v(-57.43, -19.35) * mm, "end": v(-52.7, -18.24) * mm});
            skLineSegment(sketch, "E159.MirrorCS", {"start": v(-52.7, -15.83) * mm, "end": v(-57.43, -16.94) * mm});
            skLineSegment(sketch, "E160.MirrorCS", {"start": v(-52.7, -18.24) * mm, "end": v(-47.98, -19.35) * mm});
            skLineSegment(sketch, "E161.MirrorCS", {"start": v(-47.98, -16.94) * mm, "end": v(-52.7, -15.83) * mm});
            skLineSegment(sketch, "E162.MirrorCS", {"start": v(-47.98, -19.35) * mm, "end": v(-43.39, -18.24) * mm});
            skLineSegment(sketch, "E163.MirrorCS", {"start": v(-43.39, -15.83) * mm, "end": v(-47.98, -16.94) * mm});
            skLineSegment(sketch, "E164.MirrorCS", {"start": v(-43.39, -18.24) * mm, "end": v(-38.66, -19.35) * mm});
            skLineSegment(sketch, "E165.MirrorCS", {"start": v(-38.66, -16.94) * mm, "end": v(-43.39, -15.83) * mm});
            skLineSegment(sketch, "E166.MirrorCS", {"start": v(-38.66, -19.35) * mm, "end": v(-33.29, -16.94) * mm});
            skLineSegment(sketch, "E167.MirrorCS", {"start": v(-33.29, -14.7) * mm, "end": v(-38.66, -16.94) * mm});
            skLineSegment(sketch, "E168.MirrorCS", {"start": v(-33.29, -16.94) * mm, "end": v(-33.29, -14.7) * mm});
            skLineSegment(sketch, "E169.MirrorCS", {"start": v(-57.43, -16.94) * mm, "end": v(-62.16, -15.83) * mm});
            skLineSegment(sketch, "E170.MirrorCS", {"start": v(-62.16, -7.01) * mm, "end": v(-66.07, -5.7) * mm});
            skLineSegment(sketch, "E171.MirrorCS", {"start": v(-57.43, -5.9) * mm, "end": v(-62.16, -7.01) * mm});
            skLineSegment(sketch, "E172.MirrorCS", {"start": v(-52.7, -7.01) * mm, "end": v(-57.43, -5.9) * mm});
            skLineSegment(sketch, "E173.MirrorCS", {"start": v(-47.98, -5.9) * mm, "end": v(-52.7, -7.01) * mm});
            skLineSegment(sketch, "E174.MirrorCS", {"start": v(-43.39, -7.01) * mm, "end": v(-47.98, -5.9) * mm});
            skLineSegment(sketch, "E175.MirrorCS", {"start": v(-38.66, -5.9) * mm, "end": v(-43.39, -7.01) * mm});
            skLineSegment(sketch, "E176.MirrorCS", {"start": v(-33.29, -8.14) * mm, "end": v(-38.66, -5.9) * mm});
            skLineSegment(sketch, "E177.MirrorCS", {"start": v(-38.66, -3.5) * mm, "end": v(-33.29, -5.9) * mm});
            skLineSegment(sketch, "E178.MirrorCS", {"start": v(-33.29, -5.9) * mm, "end": v(-33.29, -8.14) * mm});
            skLineSegment(sketch, "E179.MirrorCS", {"start": v(-43.39, -4.6) * mm, "end": v(-38.66, -3.5) * mm});
            skLineSegment(sketch, "E180.MirrorCS", {"start": v(-47.98, -3.5) * mm, "end": v(-43.39, -4.6) * mm});
            skLineSegment(sketch, "E181.MirrorCS", {"start": v(-52.7, -4.6) * mm, "end": v(-47.98, -3.5) * mm});
            skLineSegment(sketch, "E182.MirrorCS", {"start": v(-57.43, -3.5) * mm, "end": v(-52.7, -4.6) * mm});
            skLineSegment(sketch, "E183.MirrorCS", {"start": v(-62.16, -4.6) * mm, "end": v(-57.43, -3.5) * mm});
            skLineSegment(sketch, "E184.MirrorCS", {"start": v(-66.07, -3.5) * mm, "end": v(-62.16, -4.6) * mm});
            skLineSegment(sketch, "E185.MirrorCS", {"start": v(-66.07, -3.5) * mm, "end": v(-66.07, -5.7) * mm});
            skLineSegment(sketch, "E186.MirrorCS", {"start": v(-38.8, -22.34) * mm, "end": v(-35.78, -22.34) * mm});
            skLineSegment(sketch, "E187.MirrorCS", {"start": v(-58.9, -22.34) * mm, "end": v(-55.85, -22.34) * mm});
            skFitSpline(sketch, "E188.MirrorCS", {"points": [v(-28.93, -22.34) * mm, v(-26.8, -17.84) * mm, v(-28.93, -13.7) * mm, v(-25.63, -9.06) * mm, v(-28.93, -5.57) * mm, v(-25.94, -0.5) * mm], "startDerivative": vector(19.58, 23.39) * mm, "endDerivative": vector(25.84, 25.67) * mm});
            skFitSpline(sketch, "E189.MirrorCS", {"points": [v(-23.65, -22.34) * mm, v(-21.8, -17.84) * mm, v(-23.65, -13.7) * mm, v(-21.07, -9.06) * mm, v(-23.65, -5.57) * mm, v(-21.14, -0.5) * mm], "startDerivative": vector(16.61, 23.07) * mm, "endDerivative": vector(21.34, 25.36) * mm});
            skLineSegment(sketch, "E190.MirrorCS", {"start": v(-25.94, -0.5) * mm, "end": v(-21.14, -0.5) * mm});
            skLineSegment(sketch, "E191.MirrorCS", {"start": v(-28.93, -22.34) * mm, "end": v(-23.65, -22.34) * mm});
            skFitSpline(sketch, "E192.MirrorCS", {"points": [v(-10.63, -22.34) * mm, v(-9.04, -17.77) * mm, v(-10.63, -14.36) * mm, v(-8.91, -9.5) * mm, v(-10.63, -5.12) * mm, v(-8.57, -0.5) * mm], "startDerivative": vector(14.15, 23.8) * mm, "endDerivative": vector(16.57, 22.5) * mm});
            skLineSegment(sketch, "E193.MirrorCS", {"start": v(-6.6, -22.34) * mm, "end": v(-10.63, -22.34) * mm});
            skFitSpline(sketch, "E194.MirrorCS", {"points": [v(-6.6, -22.34) * mm, v(-4.37, -17.77) * mm, v(-6.6, -14.36) * mm, v(-4.07, -9.5) * mm, v(-6.6, -5.34) * mm, v(-3.75, -0.5) * mm], "startDerivative": vector(20.02, 24.11) * mm, "endDerivative": vector(23.18, 23.59) * mm});
            skLineSegment(sketch, "E195.MirrorCS", {"start": v(-8.57, -0.5) * mm, "end": v(-3.75, -0.5) * mm});
            skLineSegment(sketch, "E196.MirrorCS", {"start": v(-33.29, -27.45) * mm, "end": v(-27.72, -26.25) * mm});
            skLineSegment(sketch, "E197.MirrorCS", {"start": v(-27.72, -26.25) * mm, "end": v(-22.84, -27.45) * mm});
            skLineSegment(sketch, "E198.MirrorCS", {"start": v(-22.84, -27.45) * mm, "end": v(-18.15, -26.25) * mm});
            skLineSegment(sketch, "E199.MirrorCS", {"start": v(-18.15, -26.25) * mm, "end": v(-13.33, -27.45) * mm});
            skLineSegment(sketch, "E200.MirrorCS", {"start": v(-13.33, -27.45) * mm, "end": v(-8.43, -26.25) * mm});
            skLineSegment(sketch, "E201.MirrorCS", {"start": v(-8.43, -26.25) * mm, "end": v(-4.35, -27.27) * mm});
            skLineSegment(sketch, "E202.MirrorCS", {"start": v(-4.35, -27.27) * mm, "end": v(-0.44, -26.25) * mm});
            skLineSegment(sketch, "E203.MirrorCS", {"start": v(-4.35, -24.74) * mm, "end": v(-0.48, -23.54) * mm});
            skLineSegment(sketch, "E204.MirrorCS", {"start": v(-8.43, -23.54) * mm, "end": v(-4.35, -24.74) * mm});
            skLineSegment(sketch, "E205.MirrorCS", {"start": v(-13.33, -24.74) * mm, "end": v(-8.43, -23.54) * mm});
            skLineSegment(sketch, "E206.MirrorCS", {"start": v(-18.15, -23.54) * mm, "end": v(-13.33, -24.74) * mm});
            skLineSegment(sketch, "E207.MirrorCS", {"start": v(-22.84, -24.74) * mm, "end": v(-18.15, -23.54) * mm});
            skLineSegment(sketch, "E208.MirrorCS", {"start": v(-27.72, -23.54) * mm, "end": v(-22.84, -24.74) * mm});
            skLineSegment(sketch, "E209.MirrorCS", {"start": v(-33.29, -24.74) * mm, "end": v(-27.72, -23.54) * mm});
            skLineSegment(sketch, "E210", {"start": v(-59.4, -39.61) * mm, "end": v(-55.25, -39.61) * mm});
            skLineSegment(sketch, "E211", {"start": v(-38.76, -39.64) * mm, "end": v(-34.87, -39.64) * mm});
            skLineSegment(sketch, "E212", {"start": v(-33.29, -24.74) * mm, "end": v(-33.29, -27.45) * mm});
            skLineSegment(sketch, "E213", {"start": v(-0.48, -23.54) * mm, "end": v(-0.44, -26.25) * mm});
            skLineSegment(sketch, "E214", {"start": v(-33.4, -32.4) * mm, "end": v(-33.4, -35.1) * mm});
            skLineSegment(sketch, "E215", {"start": v(-33.4, -32.4) * mm, "end": v(-26.97, -31) * mm});
            skLineSegment(sketch, "E216", {"start": v(-26.97, -31) * mm, "end": v(-22.84, -32.02) * mm});
            skLineSegment(sketch, "E217", {"start": v(-22.84, -32.02) * mm, "end": v(-18.15, -31) * mm});
            skLineSegment(sketch, "E218", {"start": v(-18.15, -31) * mm, "end": v(-13.33, -32.2) * mm});
            skLineSegment(sketch, "E219", {"start": v(-13.33, -32.2) * mm, "end": v(-8.43, -31.15) * mm});
            skLineSegment(sketch, "E220", {"start": v(-8.43, -31.15) * mm, "end": v(-4.35, -32.4) * mm});
            skLineSegment(sketch, "E221", {"start": v(-4.35, -32.4) * mm, "end": v(-0.44, -30.72) * mm});
            skLineSegment(sketch, "E222", {"start": v(-33.4, -35.1) * mm, "end": v(-26.97, -33.72) * mm});
            skLineSegment(sketch, "E223", {"start": v(-26.97, -33.72) * mm, "end": v(-22.84, -35.1) * mm});
            skLineSegment(sketch, "E224", {"start": v(-22.84, -35.1) * mm, "end": v(-18.15, -34.1) * mm});
            skLineSegment(sketch, "E225", {"start": v(-18.15, -34.1) * mm, "end": v(-13.33, -35.1) * mm});
            skLineSegment(sketch, "E226", {"start": v(-13.33, -35.1) * mm, "end": v(-8.43, -34.05) * mm});
            skLineSegment(sketch, "E227", {"start": v(-8.43, -34.05) * mm, "end": v(-4.35, -35.1) * mm});
            skLineSegment(sketch, "E228", {"start": v(-4.35, -35.1) * mm, "end": v(-0.44, -33.35) * mm});
            skLineSegment(sketch, "E229", {"start": v(-0.44, -33.35) * mm, "end": v(-0.44, -30.72) * mm});
            skLineSegment(sketch, "E230", {"start": v(-66.07, -17.14) * mm, "end": v(-66.07, -19.35) * mm});
            skPoint(sketch, "E231.startSnap0", {"position": v(34.7, 22.34) * mm});
            skSolve(sketch);
        }
        {
            var Q0;
            Q0 = qSketchRegion(id + "F9", true);
            var Q1;
            {var subQ0=sQuery(id+"F9.wireOp",EDGE,"E124.MirrorCS");Q1=makeQuery(id+"F9.imprint","IMPRINT",FACE,{"disambiguationData":[TD([[makeQuery(id+"F9.imprint","IMPRINT",EDGE,{"derivedFrom":subQ0}),1.0]])]});}
            var Q2;
            Q2=makeQuery(id+"F9.imprint","IMPRINT",FACE,{"disambiguationData":[TD([[makeQuery(id+"F9.imprint","IMPRINT",EDGE,{"derivedFrom":sQuery(id+"F9.wireOp",EDGE,"E107")}),1.0]])]});
            extrude(context, id + "F10", {"entities" : qUnion([Q0, Q1, Q2]), "operationType" : NewBodyOperationType.REMOVE, "endBound" : BoundingType.UP_TO_NEXT, "oppositeDirection" : true, "depth" : 25.4 * mm});
        }
        {
            var Q0;
            Q0=makeQuery(id+"F8.boolean.opBoolean","SPLIT",FACE,{"disambiguationData":[TD([makeQuery(id+"F8.opExtrude","SWEPT_FACE",FACE,{"disambiguationData":[OSD([sQuery(id+"F7.wireOp",EDGE,"E55")])]})])],"derivedFrom":makeQuery(id+"F6.opExtrude","SWEPT_FACE",FACE,{"disambiguationData":[OSD([sQuery(id+"F5.wireOp",EDGE,"E51")])]})});
            var sketch = newSketch(context, id + "F11", { "sketchPlane" : qUnion([Q0])});
            skPoint(sketch, "E232.endSnap0", {"position": v(34.85, 0.5) * mm});
            skCircle(sketch, "E233", {"center": v(18.18, 33.01) * mm, "radius": 2.84 * mm});
            skCircle(sketch, "E234", {"center": v(18.18, 33.01) * mm, "radius": 5.9 * mm});
            skCircle(sketch, "E235", {"center": v(18.18, 33.01) * mm, "radius": 8.68 * mm});
            skEllipse(sketch, "E236", {"center": v(18.5, 11.95) * mm, "majorRadius": 5.45 * mm, "minorRadius": 2.54 * mm, "majorAxis": v(1, 0)});
            skEllipse(sketch, "E237", {"center": v(18.5, 11.95) * mm, "majorRadius": 9.36 * mm, "minorRadius": 5 * mm, "majorAxis": v(1, 0)});
            skEllipse(sketch, "E238", {"center": v(18.5, 11.95) * mm, "majorRadius": 14.09 * mm, "minorRadius": 7.98 * mm, "majorAxis": v(1, 0)});
            skCircle(sketch, "E239.MirrorC", {"center": v(50.87, 33.01) * mm, "radius": 2.84 * mm});
            skCircle(sketch, "E240.MirrorC", {"center": v(50.87, 33.01) * mm, "radius": 5.9 * mm});
            skCircle(sketch, "E241.MirrorC", {"center": v(50.87, 33.01) * mm, "radius": 8.68 * mm});
            skEllipse(sketch, "E242.MirrorC", {"center": v(50.56, 11.95) * mm, "majorRadius": 14.09 * mm, "minorRadius": 7.98 * mm, "majorAxis": v(-1, 0)});
            skEllipse(sketch, "E243.MirrorC", {"center": v(50.56, 11.95) * mm, "majorRadius": 9.36 * mm, "minorRadius": 5 * mm, "majorAxis": v(-1, 0)});
            skEllipse(sketch, "E244.MirrorC", {"center": v(50.56, 11.95) * mm, "majorRadius": 5.45 * mm, "minorRadius": 2.54 * mm, "majorAxis": v(-1, 0)});
            skSolve(sketch);
        }
        {
            var Q0;
            Q0=makeQuery(id+"F11.imprint","IMPRINT",FACE,{"disambiguationData":[TD([[makeQuery(id+"F11.imprint","IMPRINT",EDGE,{"derivedFrom":sQuery(id+"F11.wireOp",EDGE,"E233")}),1.0]])]});
            var Q1;
            Q1=makeQuery(id+"F11.imprint","IMPRINT",FACE,{"disambiguationData":[TD([[makeQuery(id+"F11.imprint","IMPRINT",EDGE,{"derivedFrom":sQuery(id+"F11.wireOp",EDGE,"E234")}),-1.0]])]});
            var Q2;
            Q2=makeQuery(id+"F11.imprint","IMPRINT",FACE,{"disambiguationData":[TD([[makeQuery(id+"F11.imprint","IMPRINT",EDGE,{"derivedFrom":sQuery(id+"F11.wireOp",EDGE,"E239.MirrorC")}),-1.0]])]});
            var Q3;
            Q3=makeQuery(id+"F11.imprint","IMPRINT",FACE,{"disambiguationData":[TD([[makeQuery(id+"F11.imprint","IMPRINT",EDGE,{"derivedFrom":sQuery(id+"F11.wireOp",EDGE,"E240.MirrorC")}),1.0]])]});
            var Q4;
            Q4=makeQuery(id+"F11.imprint","IMPRINT",FACE,{"disambiguationData":[TD([[makeQuery(id+"F11.imprint","IMPRINT",EDGE,{"derivedFrom":sQuery(id+"F11.wireOp",EDGE,"E236")}),1.0]])]});
            var Q5;
            Q5=makeQuery(id+"F11.imprint","IMPRINT",FACE,{"disambiguationData":[TD([[makeQuery(id+"F11.imprint","IMPRINT",EDGE,{"derivedFrom":sQuery(id+"F11.wireOp",EDGE,"E237")}),-1.0]])]});
            var Q6;
            Q6=makeQuery(id+"F11.imprint","IMPRINT",FACE,{"disambiguationData":[TD([[makeQuery(id+"F11.imprint","IMPRINT",EDGE,{"derivedFrom":sQuery(id+"F11.wireOp",EDGE,"E244.MirrorC")}),1.0]])]});
            var Q7;
            Q7=makeQuery(id+"F11.imprint","IMPRINT",FACE,{"disambiguationData":[TD([[makeQuery(id+"F11.imprint","IMPRINT",EDGE,{"derivedFrom":sQuery(id+"F11.wireOp",EDGE,"E242.MirrorC")}),1.0]])]});
            var Q8;
            Q8=makeQuery(id+"F11.imprint","IMPRINT",FACE,{"disambiguationData":[TD([[makeQuery(id+"F11.imprint","IMPRINT",EDGE,{"derivedFrom":sQuery(id+"F11.wireOp",EDGE,"E239.MirrorC")}),-1.0]])]});
            var Q9;
            Q9=makeQuery(id+"F11.imprint","IMPRINT",FACE,{"disambiguationData":[TD([[makeQuery(id+"F11.imprint","IMPRINT",EDGE,{"derivedFrom":sQuery(id+"F11.wireOp",EDGE,"E241.MirrorC")}),-1.0]])]});
            extrude(context, id + "F12", {"entities" : qUnion([Q0, Q1, Q2, Q3, Q4, Q5, Q6, Q7, Q8, Q9]), "operationType" : NewBodyOperationType.REMOVE, "oppositeDirection" : true, "depth" : 25.4 * mm});
        }
        {
            var Q0;
            Q0=makeQuery(id+"F8.boolean.opBoolean","SPLIT",FACE,{"disambiguationData":[TD([makeQuery(id+"F8.opExtrude","SWEPT_FACE",FACE,{"disambiguationData":[OSD([sQuery(id+"F7.wireOp",EDGE,"E58.trimOffspring")])]})])],"derivedFrom":makeQuery(id+"F6.opExtrude","SWEPT_FACE",FACE,{"disambiguationData":[OSD([sQuery(id+"F5.wireOp",EDGE,"E51")])]})});
            var sketch = newSketch(context, id + "F13", { "sketchPlane" : qUnion([Q0])});
            skLineSegment(sketch, "E245", {"start": v(34.86, -0.5) * mm, "end": v(35.15, -39.64) * mm});
            skLineSegment(sketch, "E246", {"start": v(1.46, -20.07) * mm, "end": v(68.55, -20.07) * mm});
            skCircle(sketch, "E247", {"center": v(17.06, -10.27) * mm, "radius": 2.48 * mm});
            skCircle(sketch, "E248", {"center": v(17.06, -10.27) * mm, "radius": 4.74 * mm});
            skCircle(sketch, "E249", {"center": v(17.06, -10.27) * mm, "radius": 7.66 * mm});
            skEllipse(sketch, "E250", {"center": v(16.83, -30.35) * mm, "majorRadius": 3.98 * mm, "minorRadius": 1.84 * mm, "majorAxis": v(1, 0)});
            skEllipse(sketch, "E251", {"center": v(16.83, -30.35) * mm, "majorRadius": 7.36 * mm, "minorRadius": 4 * mm, "majorAxis": v(1, 0)});
            skEllipse(sketch, "E252", {"center": v(16.83, -30.35) * mm, "majorRadius": 12.96 * mm, "minorRadius": 6.99 * mm, "majorAxis": v(1, 0)});
            skEllipse(sketch, "E253.MirrorC", {"center": v(53.32, -30.08) * mm, "majorRadius": 3.98 * mm, "minorRadius": 1.84 * mm, "majorAxis": v(-1, -0.01)});
            skEllipse(sketch, "E254.MirrorC", {"center": v(53.32, -30.08) * mm, "majorRadius": 7.36 * mm, "minorRadius": 4 * mm, "majorAxis": v(-1, -0.01)});
            skEllipse(sketch, "E255.MirrorC", {"center": v(53.32, -30.08) * mm, "majorRadius": 12.96 * mm, "minorRadius": 6.99 * mm, "majorAxis": v(-1, -0.01)});
            skCircle(sketch, "E256.MirrorC", {"center": v(52.8, -10) * mm, "radius": 2.48 * mm});
            skCircle(sketch, "E257.MirrorC", {"center": v(52.8, -10) * mm, "radius": 4.74 * mm});
            skCircle(sketch, "E258.MirrorC", {"center": v(52.8, -10) * mm, "radius": 7.66 * mm});
            skSolve(sketch);
        }
        {
            var Q0;
            Q0=makeQuery(id+"F13.imprint","IMPRINT",FACE,{"disambiguationData":[TD([[makeQuery(id+"F13.imprint","IMPRINT",EDGE,{"derivedFrom":sQuery(id+"F13.wireOp",EDGE,"E247")}),1.0]])]});
            var Q1;
            Q1=makeQuery(id+"F13.imprint","IMPRINT",FACE,{"disambiguationData":[TD([[makeQuery(id+"F13.imprint","IMPRINT",EDGE,{"derivedFrom":sQuery(id+"F13.wireOp",EDGE,"E248")}),-1.0]])]});
            var Q2;
            Q2=makeQuery(id+"F13.imprint","IMPRINT",FACE,{"disambiguationData":[TD([[makeQuery(id+"F13.imprint","IMPRINT",EDGE,{"derivedFrom":sQuery(id+"F13.wireOp",EDGE,"E256.MirrorC")}),-1.0]])]});
            var Q3;
            Q3=makeQuery(id+"F13.imprint","IMPRINT",FACE,{"disambiguationData":[TD([[makeQuery(id+"F13.imprint","IMPRINT",EDGE,{"derivedFrom":sQuery(id+"F13.wireOp",EDGE,"E257.MirrorC")}),1.0]])]});
            var Q4;
            Q4=makeQuery(id+"F13.imprint","IMPRINT",FACE,{"disambiguationData":[TD([[makeQuery(id+"F13.imprint","IMPRINT",EDGE,{"derivedFrom":sQuery(id+"F13.wireOp",EDGE,"E250")}),1.0]])]});
            var Q5;
            Q5=makeQuery(id+"F13.imprint","IMPRINT",FACE,{"disambiguationData":[TD([[makeQuery(id+"F13.imprint","IMPRINT",EDGE,{"derivedFrom":sQuery(id+"F13.wireOp",EDGE,"E251")}),-1.0]])]});
            var Q6;
            Q6=makeQuery(id+"F13.imprint","IMPRINT",FACE,{"disambiguationData":[TD([[makeQuery(id+"F13.imprint","IMPRINT",EDGE,{"derivedFrom":sQuery(id+"F13.wireOp",EDGE,"E253.MirrorC")}),1.0]])]});
            var Q7;
            Q7=makeQuery(id+"F13.imprint","IMPRINT",FACE,{"disambiguationData":[TD([[makeQuery(id+"F13.imprint","IMPRINT",EDGE,{"derivedFrom":sQuery(id+"F13.wireOp",EDGE,"E254.MirrorC")}),-1.0]])]});
            extrude(context, id + "F14", {"entities" : qUnion([Q0, Q1, Q2, Q3, Q4, Q5, Q6, Q7]), "operationType" : NewBodyOperationType.REMOVE, "oppositeDirection" : true, "depth" : 25.4 * mm});
        }
        {
            var Q0;
            Q0=makeQuery(id+"F1.opExtrude","CAP_FACE",FACE,{"disambiguationData":[OSD([sQuery(id+"F0.wireOp",EDGE,"E0.bottom"),sQuery(id+"F0.wireOp",EDGE,"E0.top"),sQuery(id+"F0.wireOp",EDGE,"E0.left"),sQuery(id+"F0.wireOp",EDGE,"E0.right")])],"isStart":false});
            extrude(context, id + "F15", {"entities" : qUnion([Q0]), "operationType" : NewBodyOperationType.ADD, "oppositeDirection" : true, "depth" : 20.32 * mm});
        }
    });
